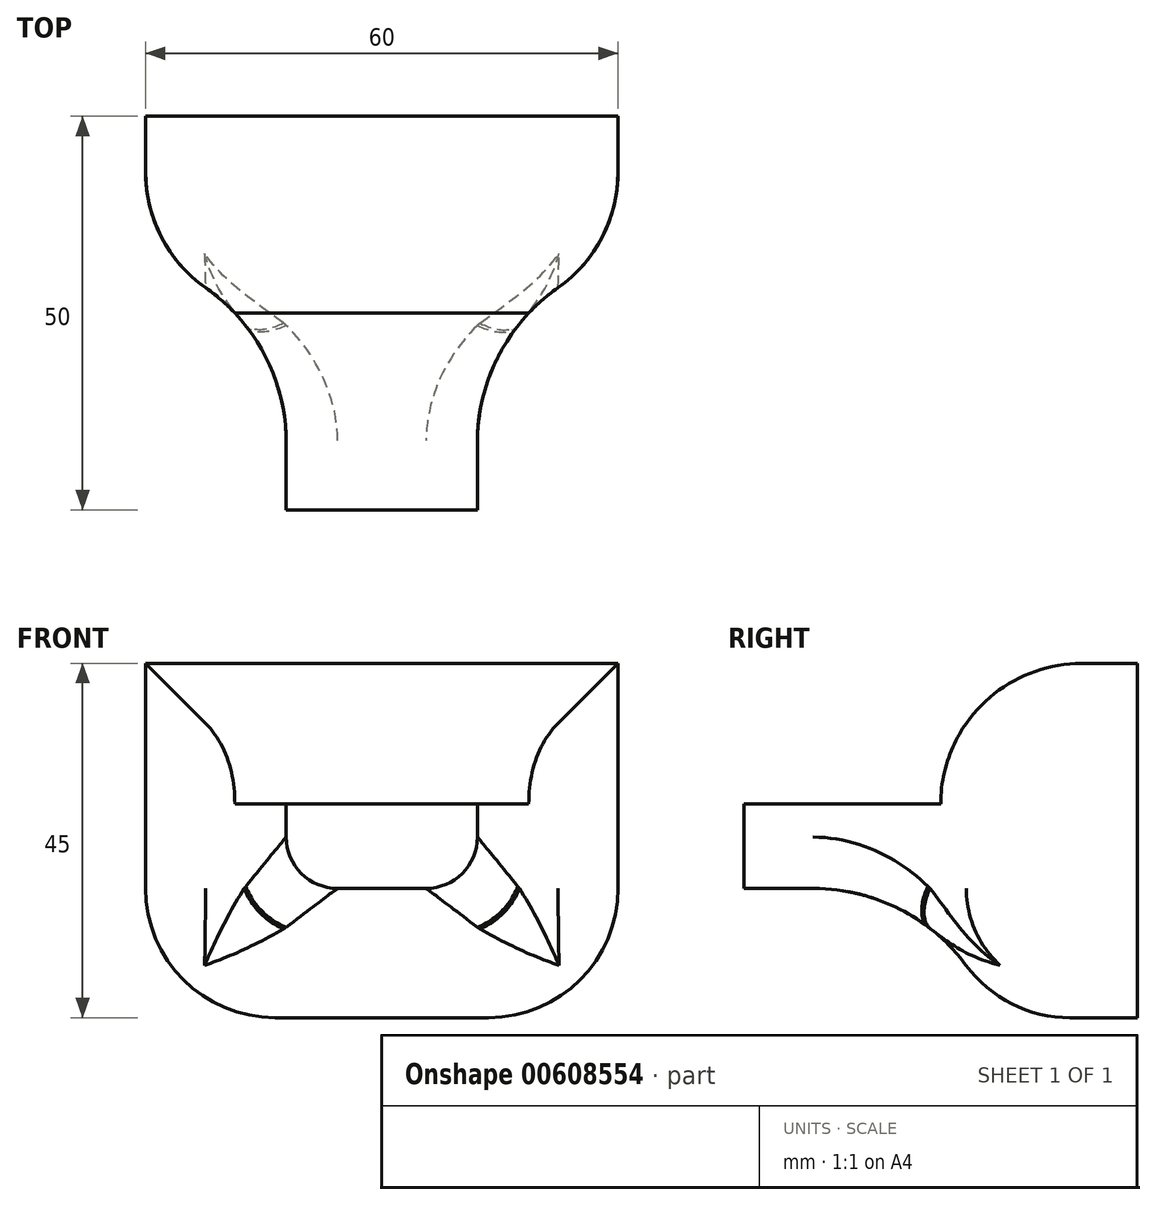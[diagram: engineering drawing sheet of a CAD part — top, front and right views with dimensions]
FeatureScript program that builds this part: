
annotation { "Feature Type Name" : "Feature", "Feature Type Description" : "" }
export const myFeature = defineFeature(function(context is Context, id is Id, definition is map)
    precondition{}
    {
        {
            var Q0;
            Q0=qCreatedBy(makeId("Front.planeOp"),FACE);
            var sketch = newSketch(context, id + "F0", { "sketchPlane" : qUnion([Q0])});
            skLineSegment(sketch, "E0.bottom", {"start": v(-45.94, -0.4) * mm, "end": v(14.06, -0.4) * mm});
            skLineSegment(sketch, "E0.top", {"start": v(-45.94, -45.4) * mm, "end": v(14.06, -45.4) * mm});
            skLineSegment(sketch, "E0.left", {"start": v(-45.94, -0.4) * mm, "end": v(-45.94, -45.4) * mm});
            skLineSegment(sketch, "E0.right", {"start": v(14.06, -0.4) * mm, "end": v(14.06, -45.4) * mm});
            skSolve(sketch);
        }
        {
            var Q0;
            Q0=makeQuery(id+"F0.imprint","IMPRINT",FACE,{"disambiguationData":[TD([[makeQuery(id+"F0.imprint","IMPRINT",EDGE,{"derivedFrom":sQuery(id+"F0.wireOp",EDGE,"E0.bottom")}),-1.0]])]});
            extrude(context, id + "F1", {"entities" : qUnion([Q0]), "depth" : 25 * mm, "offsetDistance" : 25 * mm});
        }
        {
            var Q0;
            {var subQ0=sQuery(id+"F0.wireOp",EDGE,"E0.bottom");Q0=makeQuery(id+"F1.opExtrude","CAP_EDGE",EDGE,{"disambiguationData":[OSD([subQ0]),TDD([makeQuery(id+"FgkVqZGr818QIS9_0.opExtrude","CAP_EDGE",EDGE,{"disambiguationData":[OSD([subQ0])],"isStart":false})])],"isStart":false});}
            var Q1;
            Q1=makeQuery(id+"F1.opExtrude","CAP_EDGE",EDGE,{"disambiguationData":[OSD([sQuery(id+"F0.wireOp",EDGE,"E0.left")])],"isStart":false});
            var Q2;
            Q2=makeQuery(id+"F1.opExtrude","CAP_EDGE",EDGE,{"disambiguationData":[OSD([sQuery(id+"F0.wireOp",EDGE,"E0.right")])],"isStart":false});
            fillet(context, id + "F2", {"entities" : qUnion([Q0, Q1, Q2]), "radius" : 17.87 * mm, "tangentPropagation" : true, "allowEdgeOverflow" : false});
        }
        {
            var Q0;
            {var subQ0=sQuery(id+"F0.wireOp",EDGE,"E0.bottom");Q0=makeQuery(id+"F2.opFillet","BLEND_EDGE",EDGE,{"blendedFrom":[makeQuery(id+"F1.opExtrude","CAP_EDGE",EDGE,{"disambiguationData":[OSD([subQ0]),TDD([makeQuery(id+"FgkVqZGr818QIS9_0.opExtrude","CAP_EDGE",EDGE,{"disambiguationData":[OSD([subQ0])],"isStart":false})])],"isStart":false}),makeQuery(id+"F1.opExtrude","SWEPT_FACE",FACE,{"disambiguationData":[OSD([sQuery(id+"F0.wireOp",VERTEX,"E0.bottom.start")])]})],"blendedInto":[makeQuery(id+"F1.opExtrude","SWEPT_FACE",FACE,{"disambiguationData":[OSD([sQuery(id+"F0.wireOp",VERTEX,"E0.bottom.start")])]})]});}
            var Q1;
            {var subQ0=sQuery(id+"F0.wireOp",EDGE,"E0.bottom");Q1=makeQuery(id+"F2.opFillet","BLEND_EDGE",EDGE,{"blendedFrom":[makeQuery(id+"F1.opExtrude","CAP_EDGE",EDGE,{"disambiguationData":[OSD([subQ0]),TDD([makeQuery(id+"FgkVqZGr818QIS9_0.opExtrude","CAP_EDGE",EDGE,{"disambiguationData":[OSD([subQ0])],"isStart":false})])],"isStart":false}),makeQuery(id+"F1.opExtrude","SWEPT_FACE",FACE,{"disambiguationData":[OSD([sQuery(id+"F0.wireOp",VERTEX,"E0.bottom.end")])]})],"blendedInto":[makeQuery(id+"F1.opExtrude","SWEPT_FACE",FACE,{"disambiguationData":[OSD([sQuery(id+"F0.wireOp",VERTEX,"E0.bottom.end")])]})]});}
            var Q2;
            Q2=makeQuery(id+"F2.opFillet","BLEND_EDGE",EDGE,{"blendedFrom":[makeQuery(id+"F1.opExtrude","CAP_EDGE",EDGE,{"disambiguationData":[OSD([sQuery(id+"F0.wireOp",EDGE,"E0.left")])],"isStart":false}),makeQuery(id+"F1.opExtrude","SWEPT_FACE",FACE,{"disambiguationData":[OSD([sQuery(id+"F0.wireOp",EDGE,"E0.top")])]})],"blendedInto":[makeQuery(id+"F1.opExtrude","SWEPT_FACE",FACE,{"disambiguationData":[OSD([sQuery(id+"F0.wireOp",EDGE,"E0.top")])]})]});
            var Q3;
            Q3=makeQuery(id+"F1.opExtrude","CAP_EDGE",EDGE,{"disambiguationData":[OSD([sQuery(id+"F0.wireOp",EDGE,"E0.bottom")])],"isStart":false});
            fillet(context, id + "F3", {"entities" : qUnion([Q0, Q1, Q2, Q3]), "radius" : 16.42 * mm, "tangentPropagation" : true, "allowEdgeOverflow" : false});
        }
        {
            var Q0;
            Q0=makeQuery(id+"F1.opExtrude","CAP_FACE",FACE,{"disambiguationData":[OSD([sQuery(id+"F0.wireOp",EDGE,"E0.bottom"),sQuery(id+"F0.wireOp",EDGE,"E0.top"),sQuery(id+"F0.wireOp",EDGE,"E0.left"),sQuery(id+"F0.wireOp",EDGE,"E0.right")])],"isStart":false});
            extrude(context, id + "F4", {"entities" : qUnion([Q0]), "operationType" : NewBodyOperationType.ADD, "depth" : 25 * mm, "offsetDistance" : 25 * mm});
        }
        {
            var Q0;
            {var subQ0=sQuery(id+"F0.wireOp",EDGE,"E0.right");var subQ1=sQuery(id+"F0.wireOp",EDGE,"E0.left");var subQ2=sQuery(id+"F0.wireOp",EDGE,"E0.top");var subQ3=sQuery(id+"F0.wireOp",EDGE,"E0.bottom");var subQ4=makeQuery(id+"F3.opFillet","BLEND_EDGE",EDGE,{"blendedFrom":[makeQuery(id+"F1.opExtrude","CAP_EDGE",EDGE,{"disambiguationData":[OSD([subQ3])],"isStart":false}),makeQuery(id+"F1.opExtrude","CAP_FACE",FACE,{"disambiguationData":[OSD([subQ3,subQ2,subQ1,subQ0])],"isStart":false})],"blendedInto":[makeQuery(id+"F1.opExtrude","CAP_FACE",FACE,{"disambiguationData":[OSD([subQ3,subQ2,subQ1,subQ0])],"isStart":false})]});Q0=makeQuery(id+"F4.boolean.opBoolean","MERGE",EDGE,{"derivedFrom":[subQ4,makeQuery(id+"F4.opExtrude","CAP_EDGE",EDGE,{"disambiguationData":[OSD([subQ3,subQ2,subQ1,subQ0]),TDD([subQ4])],"isStart":true})]});}
            var Q1;
            {var subQ0=sQuery(id+"F0.wireOp",EDGE,"E0.right");var subQ1=sQuery(id+"F0.wireOp",EDGE,"E0.left");var subQ2=sQuery(id+"F0.wireOp",EDGE,"E0.top");var subQ3=sQuery(id+"F0.wireOp",EDGE,"E0.bottom");var subQ4=makeQuery(id+"F2.opFillet","BLEND_EDGE",EDGE,{"blendedFrom":[makeQuery(id+"F1.opExtrude","CAP_EDGE",EDGE,{"disambiguationData":[OSD([subQ1])],"isStart":false}),makeQuery(id+"F1.opExtrude","CAP_FACE",FACE,{"disambiguationData":[OSD([subQ3,subQ2,subQ1,subQ0])],"isStart":false})],"blendedInto":[makeQuery(id+"F1.opExtrude","CAP_FACE",FACE,{"disambiguationData":[OSD([subQ3,subQ2,subQ1,subQ0])],"isStart":false})]});Q1=makeQuery(id+"F4.boolean.opBoolean","MERGE",EDGE,{"derivedFrom":[subQ4,makeQuery(id+"F4.opExtrude","CAP_EDGE",EDGE,{"disambiguationData":[OSD([subQ3,subQ2,subQ1,subQ0]),TDD([subQ4])],"isStart":true})]});}
            var Q2;
            {var subQ0=sQuery(id+"F0.wireOp",EDGE,"E0.right");var subQ1=sQuery(id+"F0.wireOp",EDGE,"E0.left");var subQ2=sQuery(id+"F0.wireOp",EDGE,"E0.top");var subQ3=sQuery(id+"F0.wireOp",EDGE,"E0.bottom");var subQ4=makeQuery(id+"F3.opFillet","BLEND_EDGE",EDGE,{"blendedFrom":[makeQuery(id+"F1.opExtrude","CAP_EDGE",EDGE,{"disambiguationData":[OSD([subQ2])],"isStart":false}),makeQuery(id+"F1.opExtrude","CAP_FACE",FACE,{"disambiguationData":[OSD([subQ3,subQ2,subQ1,subQ0])],"isStart":false})],"blendedInto":[makeQuery(id+"F1.opExtrude","CAP_FACE",FACE,{"disambiguationData":[OSD([subQ3,subQ2,subQ1,subQ0])],"isStart":false})]});Q2=makeQuery(id+"F4.boolean.opBoolean","MERGE",EDGE,{"derivedFrom":[subQ4,makeQuery(id+"F4.opExtrude","CAP_EDGE",EDGE,{"disambiguationData":[OSD([subQ3,subQ2,subQ1,subQ0]),TDD([subQ4])],"isStart":true})]});}
            var Q3;
            {var subQ0=sQuery(id+"F0.wireOp",EDGE,"E0.right");var subQ1=sQuery(id+"F0.wireOp",EDGE,"E0.left");var subQ2=sQuery(id+"F0.wireOp",EDGE,"E0.top");var subQ3=sQuery(id+"F0.wireOp",EDGE,"E0.bottom");var subQ4=makeQuery(id+"F2.opFillet","BLEND_EDGE",EDGE,{"blendedFrom":[makeQuery(id+"F1.opExtrude","CAP_EDGE",EDGE,{"disambiguationData":[OSD([subQ0])],"isStart":false}),makeQuery(id+"F1.opExtrude","CAP_FACE",FACE,{"disambiguationData":[OSD([subQ3,subQ2,subQ1,subQ0])],"isStart":false})],"blendedInto":[makeQuery(id+"F1.opExtrude","CAP_FACE",FACE,{"disambiguationData":[OSD([subQ3,subQ2,subQ1,subQ0])],"isStart":false})]});Q3=makeQuery(id+"F4.boolean.opBoolean","MERGE",EDGE,{"derivedFrom":[subQ4,makeQuery(id+"F4.opExtrude","CAP_EDGE",EDGE,{"disambiguationData":[OSD([subQ3,subQ2,subQ1,subQ0]),TDD([subQ4])],"isStart":true})]});}
            fillet(context, id + "F5", {"entities" : qUnion([Q0, Q1, Q2, Q3]), "radius" : 24.14 * mm, "tangentPropagation" : true, "allowEdgeOverflow" : false});
        }
        {
            var Q0;
            {var subQ0=sQuery(id+"F0.wireOp",EDGE,"E0.right");var subQ1=sQuery(id+"F0.wireOp",EDGE,"E0.left");var subQ2=sQuery(id+"F0.wireOp",EDGE,"E0.top");var subQ3=sQuery(id+"F0.wireOp",EDGE,"E0.bottom");var subQ4=makeQuery(id+"F1.opExtrude","CAP_FACE",FACE,{"disambiguationData":[OSD([subQ3,subQ2,subQ1,subQ0])],"isStart":false});var subQ5=makeQuery(id+"F2.opFillet","BLEND_EDGE",EDGE,{"blendedFrom":[makeQuery(id+"F1.opExtrude","CAP_EDGE",EDGE,{"disambiguationData":[OSD([subQ0])],"isStart":false}),subQ4],"blendedInto":[subQ4]});var subQ6=makeQuery(id+"F3.opFillet","BLEND_EDGE",EDGE,{"blendedFrom":[makeQuery(id+"F1.opExtrude","CAP_EDGE",EDGE,{"disambiguationData":[OSD([subQ3])],"isStart":false}),subQ4],"blendedInto":[subQ4]});Q0=makeQuery(id+"F5.opFillet","BLEND_EDGE",EDGE,{"blendedFrom":[makeQuery(id+"F4.boolean.opBoolean","MERGE",EDGE,{"derivedFrom":[subQ6,makeQuery(id+"F4.opExtrude","CAP_EDGE",EDGE,{"disambiguationData":[OSD([subQ3,subQ2,subQ1,subQ0]),TDD([subQ6])],"isStart":true})]}),makeQuery(id+"F4.boolean.opBoolean","MERGE",EDGE,{"derivedFrom":[subQ5,makeQuery(id+"F4.opExtrude","CAP_EDGE",EDGE,{"disambiguationData":[OSD([subQ3,subQ2,subQ1,subQ0]),TDD([subQ5])],"isStart":true})]})],"blendedInto":[]});}
            var Q1;
            {var subQ0=sQuery(id+"F0.wireOp",EDGE,"E0.right");var subQ1=sQuery(id+"F0.wireOp",EDGE,"E0.left");var subQ2=sQuery(id+"F0.wireOp",EDGE,"E0.top");var subQ3=sQuery(id+"F0.wireOp",EDGE,"E0.bottom");var subQ4=makeQuery(id+"F1.opExtrude","CAP_FACE",FACE,{"disambiguationData":[OSD([subQ3,subQ2,subQ1,subQ0])],"isStart":false});var subQ5=makeQuery(id+"F2.opFillet","BLEND_EDGE",EDGE,{"blendedFrom":[makeQuery(id+"F1.opExtrude","CAP_EDGE",EDGE,{"disambiguationData":[OSD([subQ0])],"isStart":false}),subQ4],"blendedInto":[subQ4]});var subQ6=makeQuery(id+"F3.opFillet","BLEND_EDGE",EDGE,{"blendedFrom":[makeQuery(id+"F1.opExtrude","CAP_EDGE",EDGE,{"disambiguationData":[OSD([subQ2])],"isStart":false}),subQ4],"blendedInto":[subQ4]});Q1=makeQuery(id+"F5.opFillet","BLEND_EDGE",EDGE,{"blendedFrom":[makeQuery(id+"F4.boolean.opBoolean","MERGE",EDGE,{"derivedFrom":[subQ6,makeQuery(id+"F4.opExtrude","CAP_EDGE",EDGE,{"disambiguationData":[OSD([subQ3,subQ2,subQ1,subQ0]),TDD([subQ6])],"isStart":true})]}),makeQuery(id+"F4.boolean.opBoolean","MERGE",EDGE,{"derivedFrom":[subQ5,makeQuery(id+"F4.opExtrude","CAP_EDGE",EDGE,{"disambiguationData":[OSD([subQ3,subQ2,subQ1,subQ0]),TDD([subQ5])],"isStart":true})]})],"blendedInto":[]});}
            var Q2;
            {var subQ0=sQuery(id+"F0.wireOp",EDGE,"E0.right");var subQ1=sQuery(id+"F0.wireOp",EDGE,"E0.left");var subQ2=sQuery(id+"F0.wireOp",EDGE,"E0.top");var subQ3=sQuery(id+"F0.wireOp",EDGE,"E0.bottom");var subQ4=makeQuery(id+"F1.opExtrude","CAP_FACE",FACE,{"disambiguationData":[OSD([subQ3,subQ2,subQ1,subQ0])],"isStart":false});var subQ5=makeQuery(id+"F2.opFillet","BLEND_EDGE",EDGE,{"blendedFrom":[makeQuery(id+"F1.opExtrude","CAP_EDGE",EDGE,{"disambiguationData":[OSD([subQ1])],"isStart":false}),subQ4],"blendedInto":[subQ4]});var subQ6=makeQuery(id+"F3.opFillet","BLEND_EDGE",EDGE,{"blendedFrom":[makeQuery(id+"F1.opExtrude","CAP_EDGE",EDGE,{"disambiguationData":[OSD([subQ3])],"isStart":false}),subQ4],"blendedInto":[subQ4]});Q2=makeQuery(id+"F5.opFillet","BLEND_EDGE",EDGE,{"blendedFrom":[makeQuery(id+"F4.boolean.opBoolean","MERGE",EDGE,{"derivedFrom":[subQ6,makeQuery(id+"F4.opExtrude","CAP_EDGE",EDGE,{"disambiguationData":[OSD([subQ3,subQ2,subQ1,subQ0]),TDD([subQ6])],"isStart":true})]}),makeQuery(id+"F4.boolean.opBoolean","MERGE",EDGE,{"derivedFrom":[subQ5,makeQuery(id+"F4.opExtrude","CAP_EDGE",EDGE,{"disambiguationData":[OSD([subQ3,subQ2,subQ1,subQ0]),TDD([subQ5])],"isStart":true})]})],"blendedInto":[]});}
            var Q3;
            {var subQ0=sQuery(id+"F0.wireOp",EDGE,"E0.right");var subQ1=sQuery(id+"F0.wireOp",EDGE,"E0.left");var subQ2=sQuery(id+"F0.wireOp",EDGE,"E0.top");var subQ3=sQuery(id+"F0.wireOp",EDGE,"E0.bottom");var subQ4=makeQuery(id+"F1.opExtrude","CAP_FACE",FACE,{"disambiguationData":[OSD([subQ3,subQ2,subQ1,subQ0])],"isStart":false});var subQ5=makeQuery(id+"F2.opFillet","BLEND_EDGE",EDGE,{"blendedFrom":[makeQuery(id+"F1.opExtrude","CAP_EDGE",EDGE,{"disambiguationData":[OSD([subQ1])],"isStart":false}),subQ4],"blendedInto":[subQ4]});var subQ6=makeQuery(id+"F3.opFillet","BLEND_EDGE",EDGE,{"blendedFrom":[makeQuery(id+"F1.opExtrude","CAP_EDGE",EDGE,{"disambiguationData":[OSD([subQ2])],"isStart":false}),subQ4],"blendedInto":[subQ4]});Q3=makeQuery(id+"F5.opFillet","BLEND_EDGE",EDGE,{"blendedFrom":[makeQuery(id+"F4.boolean.opBoolean","MERGE",EDGE,{"derivedFrom":[subQ6,makeQuery(id+"F4.opExtrude","CAP_EDGE",EDGE,{"disambiguationData":[OSD([subQ3,subQ2,subQ1,subQ0]),TDD([subQ6])],"isStart":true})]}),makeQuery(id+"F4.boolean.opBoolean","MERGE",EDGE,{"derivedFrom":[subQ5,makeQuery(id+"F4.opExtrude","CAP_EDGE",EDGE,{"disambiguationData":[OSD([subQ3,subQ2,subQ1,subQ0]),TDD([subQ5])],"isStart":true})]})],"blendedInto":[]});}
            fillet(context, id + "F6", {"entities" : qUnion([Q0, Q1, Q2, Q3]), "radius" : 6.52 * mm, "tangentPropagation" : true, "allowEdgeOverflow" : false});
        }
    });
